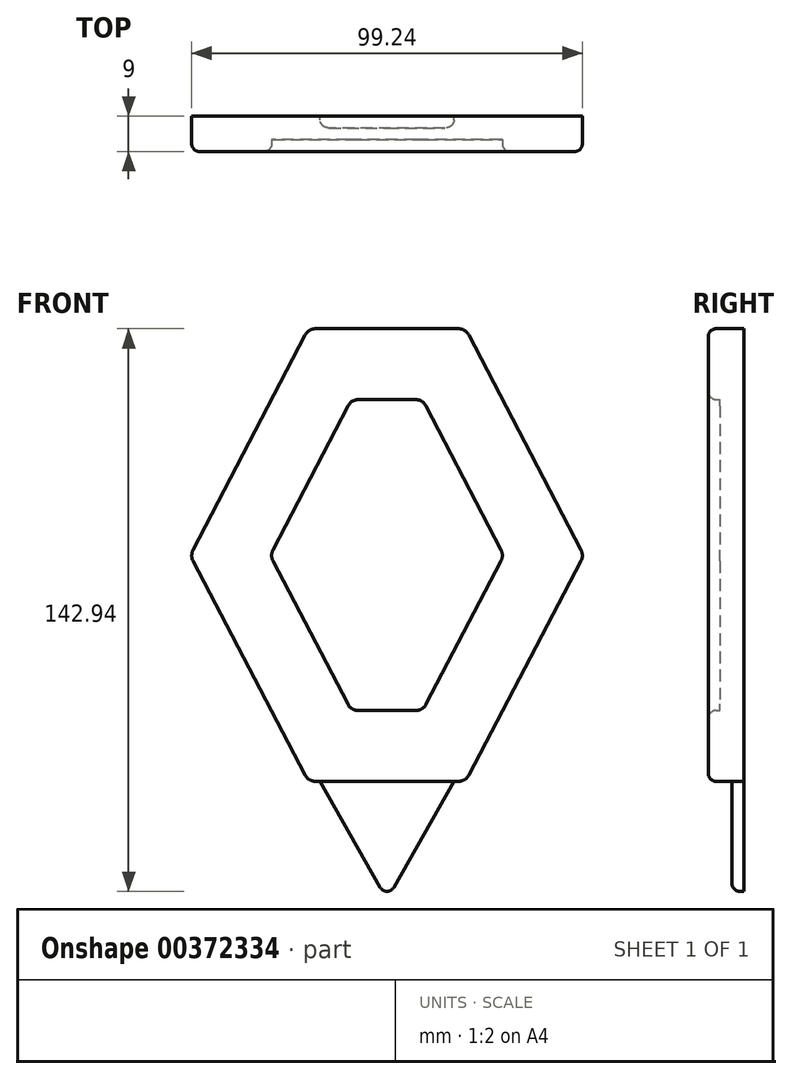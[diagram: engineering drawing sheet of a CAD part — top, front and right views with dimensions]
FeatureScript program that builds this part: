
annotation { "Feature Type Name" : "Feature", "Feature Type Description" : "" }
export const myFeature = defineFeature(function(context is Context, id is Id, definition is map)
    precondition{}
    {
        {
            var Q0;
            Q0=qCreatedBy(makeId("Front.planeOp"),FACE);
            var sketch = newSketch(context, id + "F0", { "sketchPlane" : qUnion([Q0])});
            skLineSegment(sketch, "E0", {"start": v(0, -63.02) * mm, "end": v(0, -93.02) * mm, "construction": true});
            skLineSegment(sketch, "E1", {"start": v(0, 51.98) * mm, "end": v(20, 51.98) * mm});
            skLineSegment(sketch, "E2", {"start": v(0, 51.98) * mm, "end": v(-20, 51.98) * mm});
            skLineSegment(sketch, "E3", {"start": v(0, -63.02) * mm, "end": v(-20, -63.02) * mm});
            skLineSegment(sketch, "E4", {"start": v(0, -63.02) * mm, "end": v(20, -63.02) * mm});
            skLineSegment(sketch, "E5", {"start": v(20, 51.98) * mm, "end": v(50, -5.68) * mm});
            skLineSegment(sketch, "E6", {"start": v(-20, 51.98) * mm, "end": v(-50, -5.68) * mm});
            skLineSegment(sketch, "E7", {"start": v(-50, -5.68) * mm, "end": v(-20, -63.02) * mm});
            skLineSegment(sketch, "E8", {"start": v(50, -5.68) * mm, "end": v(20, -63.02) * mm});
            skLineSegment(sketch, "E9", {"start": v(-20, -63.02) * mm, "end": v(-17, -63.02) * mm});
            skLineSegment(sketch, "E10", {"start": v(20, -63.02) * mm, "end": v(17, -63.02) * mm});
            skLineSegment(sketch, "E11", {"start": v(-17, -63.02) * mm, "end": v(0, -93.02) * mm});
            skLineSegment(sketch, "E12", {"start": v(0, -93.02) * mm, "end": v(17, -63.02) * mm});
            skSolve(sketch);
        }
        {
            var Q0;
            Q0=makeQuery(id+"F0.imprint","IMPRINT",FACE,{"disambiguationData":[TD([[makeQuery(id+"F0.imprint","IMPRINT",EDGE,{"derivedFrom":sQuery(id+"F0.wireOp",EDGE,"E1")}),-1.0]])]});
            var Q1;
            Q1=makeQuery(id+"F0.imprint","IMPRINT",FACE,{"disambiguationData":[TD([[makeQuery(id+"F0.imprint","IMPRINT",EDGE,{"derivedFrom":sQuery(id+"F0.wireOp",EDGE,"E3")}),1.0]])]});
            extrude(context, id + "F1", {"entities" : qUnion([Q0, Q1]), "depth" : 3 * mm});
        }
        {
            var Q0;
            Q0=makeQuery(id+"F1.opExtrude","CAP_FACE",FACE,{"disambiguationData":[OSD([sQuery(id+"F0.wireOp",EDGE,"E1"),sQuery(id+"F0.wireOp",EDGE,"E2"),sQuery(id+"F0.wireOp",EDGE,"E5"),sQuery(id+"F0.wireOp",EDGE,"E6"),sQuery(id+"F0.wireOp",EDGE,"E7"),sQuery(id+"F0.wireOp",EDGE,"E8"),sQuery(id+"F0.wireOp",EDGE,"E9"),sQuery(id+"F0.wireOp",EDGE,"E10"),sQuery(id+"F0.wireOp",EDGE,"E11"),sQuery(id+"F0.wireOp",EDGE,"E12")])],"isStart":false});
            var sketch = newSketch(context, id + "F2", { "sketchPlane" : qUnion([Q0])});
            skLineSegment(sketch, "E13", {"start": v(-20, 51.98) * mm, "end": v(-50, -5.68) * mm});
            skLineSegment(sketch, "E14", {"start": v(-50, -5.68) * mm, "end": v(-20, -63.02) * mm});
            skLineSegment(sketch, "E15", {"start": v(-20, -63.02) * mm, "end": v(20, -63.02) * mm});
            skLineSegment(sketch, "E16", {"start": v(20, -63.02) * mm, "end": v(50, -5.68) * mm});
            skLineSegment(sketch, "E17", {"start": v(50, -5.68) * mm, "end": v(20, 51.98) * mm});
            skLineSegment(sketch, "E18", {"start": v(20, 51.98) * mm, "end": v(-20, 51.98) * mm});
            skSolve(sketch);
        }
        {
            var Q0;
            Q0 = qSketchRegion(id + "F2", true);
            extrude(context, id + "F3", {"entities" : qUnion([Q0]), "operationType" : NewBodyOperationType.ADD, "depth" : 3 * mm});
        }
        {
            var Q0;
            Q0=makeQuery(id+"F3.opExtrude","CAP_FACE",FACE,{"disambiguationData":[OSD([sQuery(id+"F2.wireOp",EDGE,"E13"),sQuery(id+"F2.wireOp",EDGE,"E14"),sQuery(id+"F2.wireOp",EDGE,"E15"),sQuery(id+"F2.wireOp",EDGE,"E16"),sQuery(id+"F2.wireOp",EDGE,"E17"),sQuery(id+"F2.wireOp",EDGE,"E18")])],"isStart":false});
            var sketch = newSketch(context, id + "F4", { "sketchPlane" : qUnion([Q0])});
            skLineSegment(sketch, "E19", {"start": v(-20, 51.98) * mm, "end": v(-50, -5.68) * mm});
            skLineSegment(sketch, "E20", {"start": v(-50, -5.68) * mm, "end": v(-20, -63.02) * mm});
            skLineSegment(sketch, "E21", {"start": v(-20, -63.02) * mm, "end": v(20, -63.02) * mm});
            skLineSegment(sketch, "E22", {"start": v(20, -63.02) * mm, "end": v(50, -5.68) * mm});
            skLineSegment(sketch, "E23", {"start": v(50, -5.68) * mm, "end": v(20, 51.98) * mm});
            skLineSegment(sketch, "E24", {"start": v(20, 51.98) * mm, "end": v(-20, 51.98) * mm});
            skLineSegment(sketch, "E25.0", {"start": v(-29.7, -5.66) * mm, "end": v(-9.1, -45.02) * mm});
            skLineSegment(sketch, "E25.1", {"start": v(9.1, -45.02) * mm, "end": v(29.7, -5.66) * mm});
            skLineSegment(sketch, "E25.2", {"start": v(29.7, -5.66) * mm, "end": v(9.07, 33.98) * mm});
            skLineSegment(sketch, "E25.3", {"start": v(-9.1, -45.02) * mm, "end": v(9.1, -45.02) * mm});
            skLineSegment(sketch, "E25.4", {"start": v(9.07, 33.98) * mm, "end": v(-9.07, 33.98) * mm});
            skLineSegment(sketch, "E25.5", {"start": v(-9.07, 33.98) * mm, "end": v(-29.7, -5.66) * mm});
            skSolve(sketch);
        }
        {
            var Q0;
            Q0=makeQuery(id+"F4.imprint","IMPRINT",FACE,{"disambiguationData":[TD([[makeQuery(id+"F4.imprint","IMPRINT",EDGE,{"derivedFrom":sQuery(id+"F4.wireOp",EDGE,"E19")}),1.0]])]});
            extrude(context, id + "F5", {"entities" : qUnion([Q0]), "operationType" : NewBodyOperationType.ADD, "depth" : 3 * mm});
        }
        {
            var Q0;
            Q0=makeQuery(id+"F5.boolean.opBoolean","MERGE",EDGE,{"derivedFrom":[makeQuery(id+"F3.boolean.opBoolean","MERGE",EDGE,{"derivedFrom":[makeQuery(id+"F1.opExtrude","SWEPT_EDGE",EDGE,{"disambiguationData":[OSD([sQuery(id+"F0.wireOp",EDGE,"E2"),sQuery(id+"F0.wireOp",EDGE,"E6")])]}),makeQuery(id+"F3.opExtrude","SWEPT_EDGE",EDGE,{"disambiguationData":[OSD([sQuery(id+"F2.wireOp",EDGE,"E13"),sQuery(id+"F2.wireOp",EDGE,"E18")])]})]}),makeQuery(id+"F5.opExtrude","SWEPT_EDGE",EDGE,{"disambiguationData":[OSD([sQuery(id+"F4.wireOp",EDGE,"E19"),sQuery(id+"F4.wireOp",EDGE,"E24")])]})]});
            var Q1;
            Q1=makeQuery(id+"F5.boolean.opBoolean","MERGE",EDGE,{"derivedFrom":[makeQuery(id+"F3.boolean.opBoolean","MERGE",EDGE,{"derivedFrom":[makeQuery(id+"F1.opExtrude","SWEPT_EDGE",EDGE,{"disambiguationData":[OSD([sQuery(id+"F0.wireOp",EDGE,"E1"),sQuery(id+"F0.wireOp",EDGE,"E5")])]}),makeQuery(id+"F3.opExtrude","SWEPT_EDGE",EDGE,{"disambiguationData":[OSD([sQuery(id+"F2.wireOp",EDGE,"E17"),sQuery(id+"F2.wireOp",EDGE,"E18")])]})]}),makeQuery(id+"F5.opExtrude","SWEPT_EDGE",EDGE,{"disambiguationData":[OSD([sQuery(id+"F4.wireOp",EDGE,"E23"),sQuery(id+"F4.wireOp",EDGE,"E24")])]})]});
            var Q2;
            Q2=makeQuery(id+"F5.boolean.opBoolean","MERGE",EDGE,{"derivedFrom":[makeQuery(id+"F3.boolean.opBoolean","MERGE",EDGE,{"derivedFrom":[makeQuery(id+"F1.opExtrude","SWEPT_EDGE",EDGE,{"disambiguationData":[OSD([sQuery(id+"F0.wireOp",EDGE,"E6"),sQuery(id+"F0.wireOp",EDGE,"E7")])]}),makeQuery(id+"F3.opExtrude","SWEPT_EDGE",EDGE,{"disambiguationData":[OSD([sQuery(id+"F2.wireOp",EDGE,"E13"),sQuery(id+"F2.wireOp",EDGE,"E14")])]})]}),makeQuery(id+"F5.opExtrude","SWEPT_EDGE",EDGE,{"disambiguationData":[OSD([sQuery(id+"F4.wireOp",EDGE,"E19"),sQuery(id+"F4.wireOp",EDGE,"E20")])]})]});
            var Q3;
            Q3=makeQuery(id+"F5.boolean.opBoolean","MERGE",EDGE,{"derivedFrom":[makeQuery(id+"F3.boolean.opBoolean","MERGE",EDGE,{"derivedFrom":[makeQuery(id+"F1.opExtrude","SWEPT_EDGE",EDGE,{"disambiguationData":[OSD([sQuery(id+"F0.wireOp",EDGE,"E7"),sQuery(id+"F0.wireOp",EDGE,"E9")])]}),makeQuery(id+"F3.opExtrude","SWEPT_EDGE",EDGE,{"disambiguationData":[OSD([sQuery(id+"F2.wireOp",EDGE,"E14"),sQuery(id+"F2.wireOp",EDGE,"E15")])]})]}),makeQuery(id+"F5.opExtrude","SWEPT_EDGE",EDGE,{"disambiguationData":[OSD([sQuery(id+"F4.wireOp",EDGE,"E20"),sQuery(id+"F4.wireOp",EDGE,"E21")])]})]});
            var Q4;
            Q4=makeQuery(id+"F5.boolean.opBoolean","MERGE",EDGE,{"derivedFrom":[makeQuery(id+"F3.boolean.opBoolean","MERGE",EDGE,{"derivedFrom":[makeQuery(id+"F1.opExtrude","SWEPT_EDGE",EDGE,{"disambiguationData":[OSD([sQuery(id+"F0.wireOp",EDGE,"E8"),sQuery(id+"F0.wireOp",EDGE,"E10")])]}),makeQuery(id+"F3.opExtrude","SWEPT_EDGE",EDGE,{"disambiguationData":[OSD([sQuery(id+"F2.wireOp",EDGE,"E15"),sQuery(id+"F2.wireOp",EDGE,"E16")])]})]}),makeQuery(id+"F5.opExtrude","SWEPT_EDGE",EDGE,{"disambiguationData":[OSD([sQuery(id+"F4.wireOp",EDGE,"E21"),sQuery(id+"F4.wireOp",EDGE,"E22")])]})]});
            var Q5;
            Q5=makeQuery(id+"F5.boolean.opBoolean","MERGE",EDGE,{"derivedFrom":[makeQuery(id+"F3.boolean.opBoolean","MERGE",EDGE,{"derivedFrom":[makeQuery(id+"F1.opExtrude","SWEPT_EDGE",EDGE,{"disambiguationData":[OSD([sQuery(id+"F0.wireOp",EDGE,"E5"),sQuery(id+"F0.wireOp",EDGE,"E8")])]}),makeQuery(id+"F3.opExtrude","SWEPT_EDGE",EDGE,{"disambiguationData":[OSD([sQuery(id+"F2.wireOp",EDGE,"E16"),sQuery(id+"F2.wireOp",EDGE,"E17")])]})]}),makeQuery(id+"F5.opExtrude","SWEPT_EDGE",EDGE,{"disambiguationData":[OSD([sQuery(id+"F4.wireOp",EDGE,"E22"),sQuery(id+"F4.wireOp",EDGE,"E23")])]})]});
            var Q6;
            Q6=makeQuery(id+"F5.opExtrude","SWEPT_EDGE",EDGE,{"disambiguationData":[OSD([sQuery(id+"F4.wireOp",EDGE,"E25.2"),sQuery(id+"F4.wireOp",EDGE,"E25.4")])]});
            var Q7;
            Q7=makeQuery(id+"F5.opExtrude","SWEPT_EDGE",EDGE,{"disambiguationData":[OSD([sQuery(id+"F4.wireOp",EDGE,"E25.1"),sQuery(id+"F4.wireOp",EDGE,"E25.2")])]});
            var Q8;
            Q8=makeQuery(id+"F5.opExtrude","SWEPT_EDGE",EDGE,{"disambiguationData":[OSD([sQuery(id+"F4.wireOp",EDGE,"E25.4"),sQuery(id+"F4.wireOp",EDGE,"E25.5")])]});
            var Q9;
            Q9=makeQuery(id+"F5.opExtrude","SWEPT_EDGE",EDGE,{"disambiguationData":[OSD([sQuery(id+"F4.wireOp",EDGE,"E25.0"),sQuery(id+"F4.wireOp",EDGE,"E25.5")])]});
            var Q10;
            Q10=makeQuery(id+"F5.opExtrude","SWEPT_EDGE",EDGE,{"disambiguationData":[OSD([sQuery(id+"F4.wireOp",EDGE,"E25.0"),sQuery(id+"F4.wireOp",EDGE,"E25.3")])]});
            var Q11;
            Q11=makeQuery(id+"F5.opExtrude","SWEPT_EDGE",EDGE,{"disambiguationData":[OSD([sQuery(id+"F4.wireOp",EDGE,"E25.1"),sQuery(id+"F4.wireOp",EDGE,"E25.3")])]});
            fillet(context, id + "F6", {"entities" : qUnion([Q0, Q1, Q2, Q3, Q4, Q5, Q6, Q7, Q8, Q9, Q10, Q11]), "radius" : 3 * mm, "tangentPropagation" : true, "allowEdgeOverflow" : false});
        }
        {
            var Q0;
            Q0=makeQuery(id+"F5.opExtrude","CAP_EDGE",EDGE,{"disambiguationData":[OSD([sQuery(id+"F4.wireOp",EDGE,"E19")])],"isStart":false});
            var Q1;
            Q1=makeQuery(id+"F5.opExtrude","CAP_EDGE",EDGE,{"disambiguationData":[OSD([sQuery(id+"F4.wireOp",EDGE,"E25.5")])],"isStart":false});
            var Q2;
            Q2=makeQuery(id+"F1.opExtrude","CAP_EDGE",EDGE,{"disambiguationData":[OSD([sQuery(id+"F0.wireOp",EDGE,"E12")])],"isStart":false});
            var Q3;
            Q3=makeQuery(id+"F1.opExtrude","CAP_EDGE",EDGE,{"disambiguationData":[OSD([sQuery(id+"F0.wireOp",EDGE,"E11")])],"isStart":false});
            var Q4;
            Q4=makeQuery(id+"F1.opExtrude","SWEPT_EDGE",EDGE,{"disambiguationData":[OSD([sQuery(id+"F0.wireOp",EDGE,"E11"),sQuery(id+"F0.wireOp",EDGE,"E12")])]});
            fillet(context, id + "F7", {"entities" : qUnion([Q0, Q1, Q2, Q3, Q4]), "radius" : 2 * mm, "tangentPropagation" : true, "allowEdgeOverflow" : false});
        }
    });
